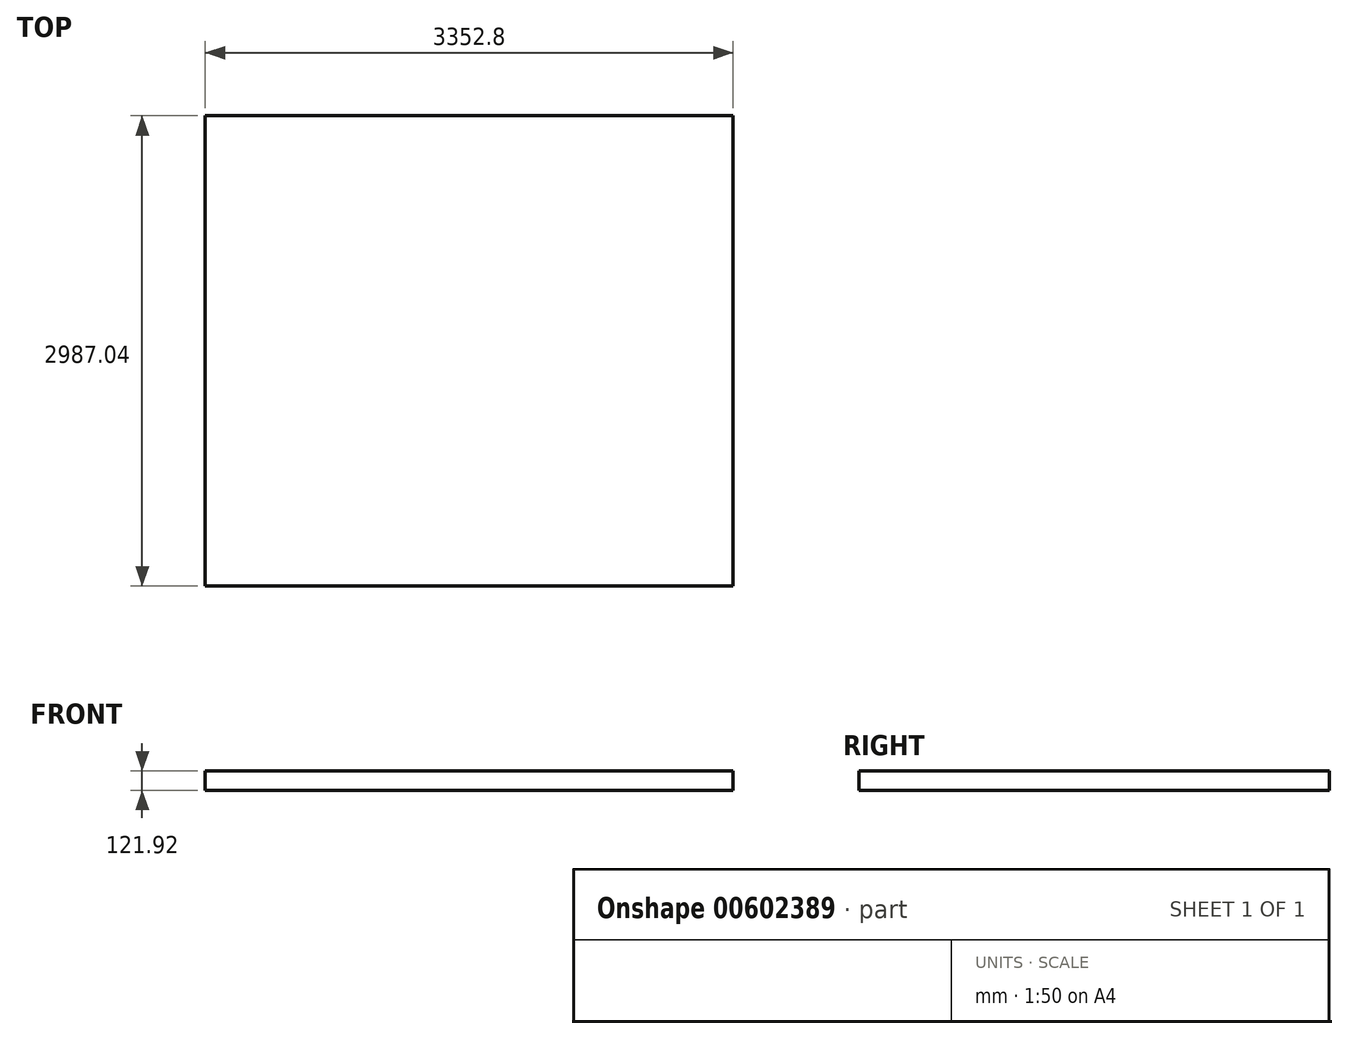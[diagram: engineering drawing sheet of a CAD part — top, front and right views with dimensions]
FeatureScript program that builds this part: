
annotation { "Feature Type Name" : "Feature", "Feature Type Description" : "" }
export const myFeature = defineFeature(function(context is Context, id is Id, definition is map)
    precondition{}
    {
        {
            var Q0;
            Q0=qCreatedBy(makeId("Top.planeOp"),FACE);
            var sketch = newSketch(context, id + "F0", { "sketchPlane" : qUnion([Q0])});
            skLineSegment(sketch, "E0.bottom", {"start": v(-1676.4, 1493.52) * mm, "end": v(1676.4, 1493.52) * mm});
            skLineSegment(sketch, "E0.top", {"start": v(-1676.4, -1493.52) * mm, "end": v(1676.4, -1493.52) * mm});
            skLineSegment(sketch, "E0.left", {"start": v(-1676.4, 1493.52) * mm, "end": v(-1676.4, -1493.52) * mm});
            skLineSegment(sketch, "E0.right", {"start": v(1676.4, 1493.52) * mm, "end": v(1676.4, -1493.52) * mm});
            skPoint(sketch, "E0.middle", {"position": v(0, 0) * mm});
            skSolve(sketch);
        }
        {
            var Q0;
            Q0=makeQuery(id+"F0.imprint","IMPRINT",FACE,{"disambiguationData":[TD([[makeQuery(id+"F0.imprint","IMPRINT",EDGE,{"derivedFrom":sQuery(id+"F0.wireOp",EDGE,"E0.bottom")}),-1.0]])]});
            extrude(context, id + "F1", {"entities" : qUnion([Q0]), "depth" : 121.92 * mm, "offsetDistance" : 30.48 * mm});
        }
    });
